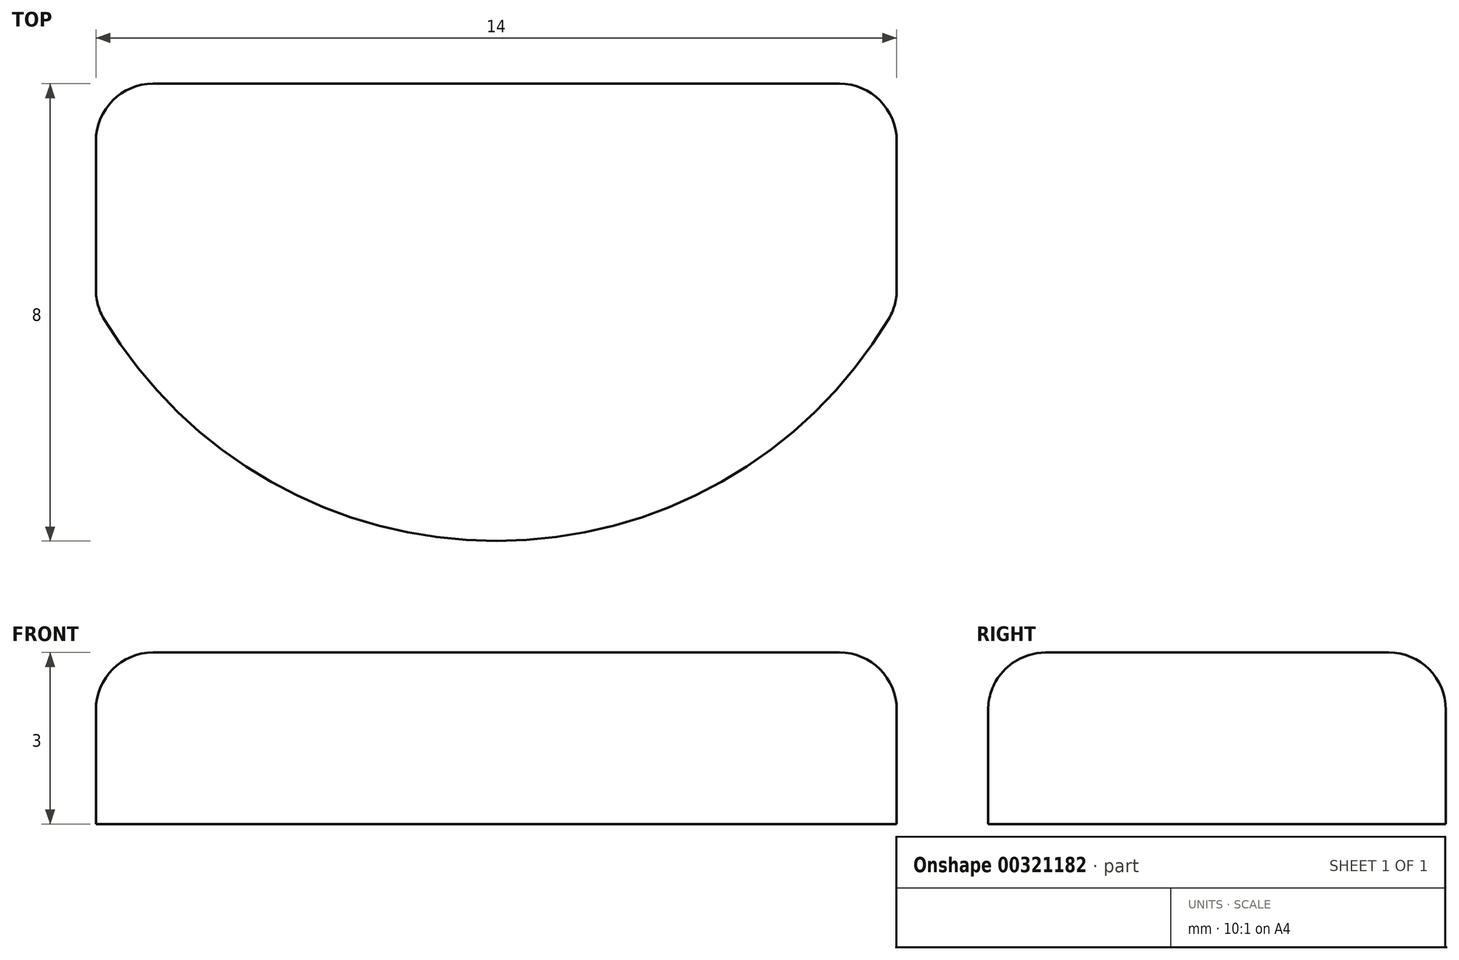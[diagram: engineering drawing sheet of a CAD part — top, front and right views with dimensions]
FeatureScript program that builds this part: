
annotation { "Feature Type Name" : "Feature", "Feature Type Description" : "" }
export const myFeature = defineFeature(function(context is Context, id is Id, definition is map)
    precondition{}
    {
        {
            var Q0;
            Q0=qCreatedBy(makeId("Top.planeOp"),FACE);
            var sketch = newSketch(context, id + "F0", { "sketchPlane" : qUnion([Q0])});
            skArc(sketch, "E0", {"start": v(-7, -3.87) * mm, "mid": v(0, -8) * mm, "end": v(7, -3.87) * mm});
            skLineSegment(sketch, "E1", {"start": v(-7, 0) * mm, "end": v(7, 0) * mm});
            skLineSegment(sketch, "E2", {"start": v(0, 0) * mm, "end": v(-7, 0) * mm});
            skLineSegment(sketch, "E3", {"start": v(-7, 0) * mm, "end": v(-7, -3.87) * mm});
            skArc(sketch, "E4.MirrorCS", {"start": v(7, -3.87) * mm, "mid": v(0, -8) * mm, "end": v(-7, -3.87) * mm});
            skLineSegment(sketch, "E5.MirrorCS", {"start": v(7, 0) * mm, "end": v(7, -3.87) * mm});
            skSolve(sketch);
        }
        {
            var Q0;
            Q0=makeQuery(id+"F0.imprint","IMPRINT",FACE,{"disambiguationData":[TD([[makeQuery(id+"F0.imprint","IMPRINT",EDGE,{"derivedFrom":sQuery(id+"F0.wireOp",EDGE,"E1")}),-1.0]])]});
            extrude(context, id + "F1", {"entities" : qUnion([Q0]), "depth" : 3 * mm});
        }
        {
            var Q0;
            Q0=makeQuery(id+"F1.opExtrude","CAP_EDGE",EDGE,{"disambiguationData":[OSD([sQuery(id+"F0.wireOp",EDGE,"E3")])],"isStart":false});
            var Q1;
            Q1=makeQuery(id+"F1.opExtrude","CAP_EDGE",EDGE,{"disambiguationData":[OSD([sQuery(id+"F0.wireOp",EDGE,"E1"),sQuery(id+"F0.wireOp",EDGE,"E2")])],"isStart":false});
            var Q2;
            Q2=makeQuery(id+"F1.opExtrude","CAP_EDGE",EDGE,{"disambiguationData":[OSD([sQuery(id+"F0.wireOp",EDGE,"E5.MirrorCS")])],"isStart":false});
            var Q3;
            Q3=makeQuery(id+"F1.opExtrude","CAP_EDGE",EDGE,{"disambiguationData":[OSD([sQuery(id+"F0.wireOp",EDGE,"E0")])],"isStart":false});
            var Q4;
            Q4=makeQuery(id+"F1.opExtrude","SWEPT_EDGE",EDGE,{"disambiguationData":[OSD([sQuery(id+"F0.wireOp",EDGE,"E3"),sQuery(id+"F0.wireOp",EDGE,"E0")])]});
            var Q5;
            Q5=makeQuery(id+"F1.opExtrude","SWEPT_EDGE",EDGE,{"disambiguationData":[OSD([sQuery(id+"F0.wireOp",EDGE,"E2"),sQuery(id+"F0.wireOp",EDGE,"E3")])]});
            var Q6;
            Q6=makeQuery(id+"F1.opExtrude","SWEPT_EDGE",EDGE,{"disambiguationData":[OSD([sQuery(id+"F0.wireOp",EDGE,"E5.MirrorCS"),sQuery(id+"F0.wireOp",EDGE,"E0")])]});
            var Q7;
            Q7=makeQuery(id+"F1.opExtrude","SWEPT_EDGE",EDGE,{"disambiguationData":[OSD([sQuery(id+"F0.wireOp",EDGE,"E1"),sQuery(id+"F0.wireOp",EDGE,"E5.MirrorCS")])]});
            fillet(context, id + "F2", {"entities" : qUnion([Q0, Q1, Q2, Q3, Q4, Q5, Q6, Q7]), "radius" : 1 * mm, "tangentPropagation" : true, "allowEdgeOverflow" : false});
        }
    });
